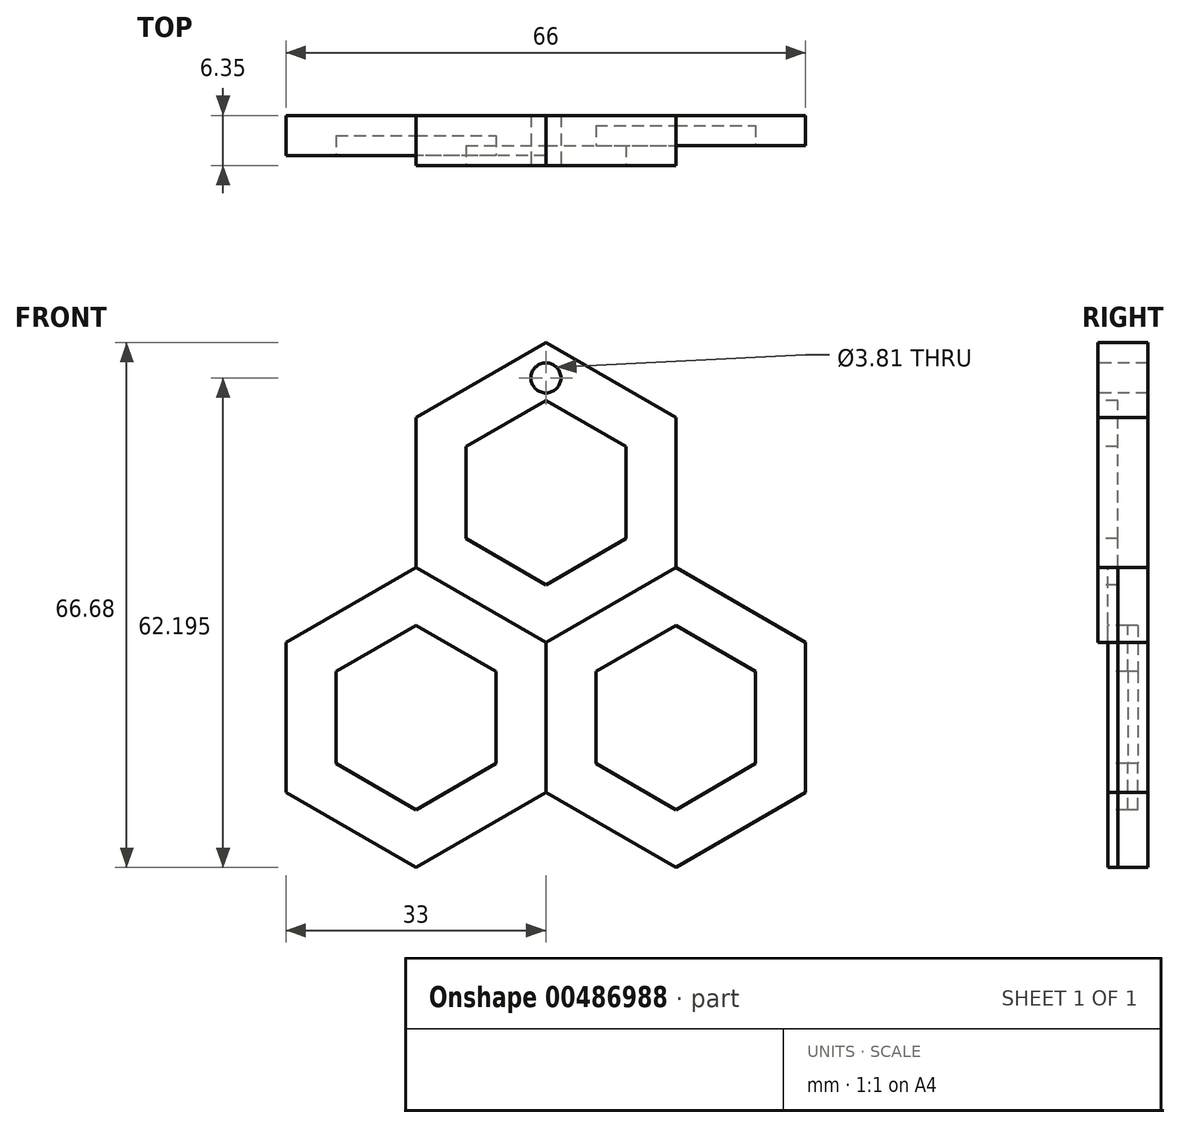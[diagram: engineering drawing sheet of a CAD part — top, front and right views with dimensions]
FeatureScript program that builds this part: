
annotation { "Feature Type Name" : "Feature", "Feature Type Description" : "" }
export const myFeature = defineFeature(function(context is Context, id is Id, definition is map)
    precondition{}
    {
        {
            var Q0;
            Q0=qCreatedBy(makeId("Front.planeOp"),FACE);
            var sketch = newSketch(context, id + "F0", { "sketchPlane" : qUnion([Q0])});
            skLineSegment(sketch, "E0", {"start": v(16.5, 9.52) * mm, "end": v(16.5, 28.57) * mm});
            skLineSegment(sketch, "E1", {"start": v(16.5, 28.57) * mm, "end": v(0, 38.1) * mm});
            skLineSegment(sketch, "E2.MirrorCS", {"start": v(-16.5, 9.52) * mm, "end": v(-16.5, 28.57) * mm});
            skLineSegment(sketch, "E3.MirrorCS", {"start": v(0, 0) * mm, "end": v(-16.5, 9.52) * mm});
            skLineSegment(sketch, "E4", {"start": v(0, 38.1) * mm, "end": v(0, 0) * mm, "construction": true});
            skLineSegment(sketch, "E5", {"start": v(16.5, 28.57) * mm, "end": v(-16.5, 28.58) * mm, "construction": true});
            skLineSegment(sketch, "E6", {"start": v(-16.5, 9.52) * mm, "end": v(16.5, 9.52) * mm, "construction": true});
            skLineSegment(sketch, "E7", {"start": v(0, 0) * mm, "end": v(16.5, 9.52) * mm});
            skLineSegment(sketch, "E8", {"start": v(-16.5, 28.57) * mm, "end": v(0, 38.1) * mm});
            skSolve(sketch);
        }
        {
            var Q0;
            Q0=qCreatedBy(makeId("Front.planeOp"),FACE);
            var sketch = newSketch(context, id + "F1", { "sketchPlane" : qUnion([Q0])});
            skLineSegment(sketch, "E9", {"start": v(0, 0) * mm, "end": v(16.5, 9.53) * mm});
            skLineSegment(sketch, "E10", {"start": v(16.5, 9.53) * mm, "end": v(33, 0) * mm});
            skLineSegment(sketch, "E11", {"start": v(33, 0) * mm, "end": v(33, -19.05) * mm});
            skLineSegment(sketch, "E12", {"start": v(33, -19.05) * mm, "end": v(16.5, -28.58) * mm});
            skLineSegment(sketch, "E13", {"start": v(16.5, -28.58) * mm, "end": v(0, -19.05) * mm});
            skLineSegment(sketch, "E14", {"start": v(0, -19.05) * mm, "end": v(0, 0) * mm});
            skLineSegment(sketch, "E15", {"start": v(16.5, -28.58) * mm, "end": v(16.5, 9.53) * mm, "construction": true});
            skLineSegment(sketch, "E16", {"start": v(0, 0) * mm, "end": v(33, 0) * mm, "construction": true});
            skLineSegment(sketch, "E17", {"start": v(33, -19.05) * mm, "end": v(0, -19.05) * mm, "construction": true});
            skSolve(sketch);
        }
        {
            var Q0;
            Q0=qCreatedBy(makeId("Front.planeOp"),FACE);
            var sketch = newSketch(context, id + "F2", { "sketchPlane" : qUnion([Q0])});
            skLineSegment(sketch, "E18.MirrorCS", {"start": v(-16.5, -28.58) * mm, "end": v(0, -19.05) * mm});
            skLineSegment(sketch, "E19.MirrorCS", {"start": v(0, 0) * mm, "end": v(-16.5, 9.52) * mm});
            skLineSegment(sketch, "E20", {"start": v(0, 0) * mm, "end": v(0, -19.05) * mm});
            skLineSegment(sketch, "E21", {"start": v(-16.5, 9.52) * mm, "end": v(-16.5, -28.57) * mm, "construction": true});
            skLineSegment(sketch, "E22", {"start": v(0, -19.05) * mm, "end": v(-33, -19.05) * mm, "construction": true});
            skLineSegment(sketch, "E23", {"start": v(-33, 0) * mm, "end": v(0, 0) * mm, "construction": true});
            skLineSegment(sketch, "E24.MirrorCS", {"start": v(-33, 0) * mm, "end": v(-16.5, 9.52) * mm});
            skLineSegment(sketch, "E25.MirrorCS", {"start": v(-33, 0) * mm, "end": v(-33, -19.05) * mm});
            skLineSegment(sketch, "E26.MirrorCS", {"start": v(-16.5, -28.57) * mm, "end": v(-33, -19.05) * mm});
            skSolve(sketch);
        }
        {
            var Q0;
            Q0 = qSketchRegion(id + "F0", true);
            extrude(context, id + "F3", {"entities" : qUnion([Q0]), "depth" : 6.35 * mm});
        }
        {
            var Q0;
            Q0 = qSketchRegion(id + "F1", true);
            extrude(context, id + "F4", {"entities" : qUnion([Q0]), "operationType" : NewBodyOperationType.ADD, "depth" : 3.8 * mm});
        }
        {
            var Q0;
            Q0 = qSketchRegion(id + "F2", true);
            extrude(context, id + "F5", {"entities" : qUnion([Q0]), "operationType" : NewBodyOperationType.ADD, "depth" : 5.08 * mm});
        }
        {
            var Q0;
            Q0=makeQuery(id+"F3.opExtrude","CAP_FACE",FACE,{"disambiguationData":[OSD([sQuery(id+"F0.wireOp",EDGE,"E0"),sQuery(id+"F0.wireOp",EDGE,"E1"),sQuery(id+"F0.wireOp",EDGE,"E2.MirrorCS"),sQuery(id+"F0.wireOp",EDGE,"E3.MirrorCS"),sQuery(id+"F0.wireOp",EDGE,"E7"),sQuery(id+"F0.wireOp",EDGE,"E8")])],"isStart":false});
            var sketch = newSketch(context, id + "F6", { "sketchPlane" : qUnion([Q0])});
            skLineSegment(sketch, "E27.0", {"start": v(-10.15, 13.2) * mm, "end": v(-10.15, 24.9) * mm});
            skLineSegment(sketch, "E27.1", {"start": v(10.15, 24.9) * mm, "end": v(0, 30.77) * mm});
            skLineSegment(sketch, "E27.2", {"start": v(10.15, 13.2) * mm, "end": v(10.15, 24.9) * mm});
            skLineSegment(sketch, "E27.3", {"start": v(-10.15, 24.9) * mm, "end": v(0, 30.77) * mm});
            skLineSegment(sketch, "E27.4", {"start": v(0, 7.33) * mm, "end": v(10.15, 13.2) * mm});
            skLineSegment(sketch, "E27.5", {"start": v(0, 7.33) * mm, "end": v(-10.15, 13.2) * mm});
            skSolve(sketch);
        }
        {
            var Q0;
            Q0 = qSketchRegion(id + "F6", true);
            extrude(context, id + "F7", {"entities" : qUnion([Q0]), "operationType" : NewBodyOperationType.REMOVE, "oppositeDirection" : true, "depth" : 2.54 * mm});
        }
        {
            var Q0;
            Q0=makeQuery(id+"F5.opExtrude","CAP_FACE",FACE,{"disambiguationData":[OSD([sQuery(id+"F2.wireOp",EDGE,"E18.MirrorCS"),sQuery(id+"F2.wireOp",EDGE,"E19.MirrorCS"),sQuery(id+"F2.wireOp",EDGE,"E20"),sQuery(id+"F2.wireOp",EDGE,"E24.MirrorCS"),sQuery(id+"F2.wireOp",EDGE,"E25.MirrorCS"),sQuery(id+"F2.wireOp",EDGE,"E26.MirrorCS")])],"isStart":false});
            var sketch = newSketch(context, id + "F8", { "sketchPlane" : qUnion([Q0])});
            skLineSegment(sketch, "E28.0", {"start": v(-26.65, -3.67) * mm, "end": v(-26.65, -15.38) * mm});
            skLineSegment(sketch, "E28.1", {"start": v(-6.35, -3.67) * mm, "end": v(-16.5, 2.2) * mm});
            skLineSegment(sketch, "E28.2", {"start": v(-6.35, -3.67) * mm, "end": v(-6.35, -15.38) * mm});
            skLineSegment(sketch, "E28.3", {"start": v(-26.65, -3.67) * mm, "end": v(-16.5, 2.2) * mm});
            skLineSegment(sketch, "E28.4", {"start": v(-16.5, -21.24) * mm, "end": v(-6.35, -15.38) * mm});
            skLineSegment(sketch, "E28.5", {"start": v(-16.5, -21.24) * mm, "end": v(-26.65, -15.38) * mm});
            skSolve(sketch);
        }
        {
            var Q0;
            Q0 = qSketchRegion(id + "F8", true);
            extrude(context, id + "F9", {"entities" : qUnion([Q0]), "operationType" : NewBodyOperationType.REMOVE, "oppositeDirection" : true, "depth" : 2.54 * mm});
        }
        {
            var Q0;
            Q0=makeQuery(id+"F4.opExtrude","CAP_FACE",FACE,{"disambiguationData":[OSD([sQuery(id+"F1.wireOp",EDGE,"E9"),sQuery(id+"F1.wireOp",EDGE,"E10"),sQuery(id+"F1.wireOp",EDGE,"E11"),sQuery(id+"F1.wireOp",EDGE,"E12"),sQuery(id+"F1.wireOp",EDGE,"E13"),sQuery(id+"F1.wireOp",EDGE,"E14")])],"isStart":false});
            var sketch = newSketch(context, id + "F10", { "sketchPlane" : qUnion([Q0])});
            skLineSegment(sketch, "E29.0", {"start": v(6.35, -3.67) * mm, "end": v(16.5, 2.2) * mm});
            skLineSegment(sketch, "E29.1", {"start": v(26.65, -3.67) * mm, "end": v(26.65, -15.38) * mm});
            skLineSegment(sketch, "E29.2", {"start": v(26.65, -15.38) * mm, "end": v(16.5, -21.24) * mm});
            skLineSegment(sketch, "E29.3", {"start": v(16.5, 2.2) * mm, "end": v(26.65, -3.67) * mm});
            skLineSegment(sketch, "E29.4", {"start": v(16.5, -21.24) * mm, "end": v(6.35, -15.38) * mm});
            skLineSegment(sketch, "E29.5", {"start": v(6.35, -3.67) * mm, "end": v(6.35, -15.38) * mm});
            skSolve(sketch);
        }
        {
            var Q0;
            Q0 = qSketchRegion(id + "F10", true);
            extrude(context, id + "F11", {"entities" : qUnion([Q0]), "operationType" : NewBodyOperationType.REMOVE, "oppositeDirection" : true, "depth" : 2.54 * mm});
        }
        {
            var Q0;
            Q0=qCreatedBy(makeId("Front.planeOp"),FACE);
            var sketch = newSketch(context, id + "F12", { "sketchPlane" : qUnion([Q0])});
            skLineSegment(sketch, "E30", {"start": v(-7.29, -23.37) * mm, "end": v(0, -30.66) * mm});
            skLineSegment(sketch, "E31", {"start": v(0, -30.66) * mm, "end": v(7.29, -23.37) * mm});
            skLineSegment(sketch, "E32", {"start": v(-7.29, -23.37) * mm, "end": v(0, -19.37) * mm});
            skLineSegment(sketch, "E33", {"start": v(0, -19.37) * mm, "end": v(7.29, -23.37) * mm});
            skLineSegment(sketch, "E34", {"start": v(-7.29, -23.37) * mm, "end": v(7.29, -23.37) * mm, "construction": true});
            skLineSegment(sketch, "E35", {"start": v(0, -30.66) * mm, "end": v(0, -19.37) * mm, "construction": true});
            skSolve(sketch);
        }
        {
            var Q0;
            Q0 = qSketchRegion(id + "F12", true);
            extrude(context, id + "F13", {"entities" : qUnion([Q0]), "depth" : 1.27 * mm});
        }
        {
            var Q0;
            Q0=makeQuery(id+"F13.opExtrude","SWEPT_BODY",BODY,{"disambiguationData":[OSD([sQuery(id+"F12.wireOp",EDGE,"E30"),sQuery(id+"F12.wireOp",EDGE,"E31"),sQuery(id+"F12.wireOp",EDGE,"E32"),sQuery(id+"F12.wireOp",EDGE,"E33")])]});
            deleteBodies(context, id + "F14", {"entities" : qUnion([Q0])});
        }
        {
            var Q0;
            Q0=makeQuery(id+"F3.opExtrude","CAP_FACE",FACE,{"disambiguationData":[OSD([sQuery(id+"F0.wireOp",EDGE,"E0"),sQuery(id+"F0.wireOp",EDGE,"E1"),sQuery(id+"F0.wireOp",EDGE,"E2.MirrorCS"),sQuery(id+"F0.wireOp",EDGE,"E3.MirrorCS"),sQuery(id+"F0.wireOp",EDGE,"E7"),sQuery(id+"F0.wireOp",EDGE,"E8")])],"isStart":false});
            var sketch = newSketch(context, id + "F15", { "sketchPlane" : qUnion([Q0])});
            skLineSegment(sketch, "E36", {"start": v(0, 30.77) * mm, "end": v(0, 38.1) * mm, "construction": true});
            skCircle(sketch, "E37", {"center": v(0, 33.61) * mm, "radius": 1.9 * mm});
            skSolve(sketch);
        }
        {
            var Q0;
            Q0 = qSketchRegion(id + "F15", true);
            extrude(context, id + "F16", {"entities" : qUnion([Q0]), "operationType" : NewBodyOperationType.REMOVE, "oppositeDirection" : true, "depth" : 25.4 * mm});
        }
    });
